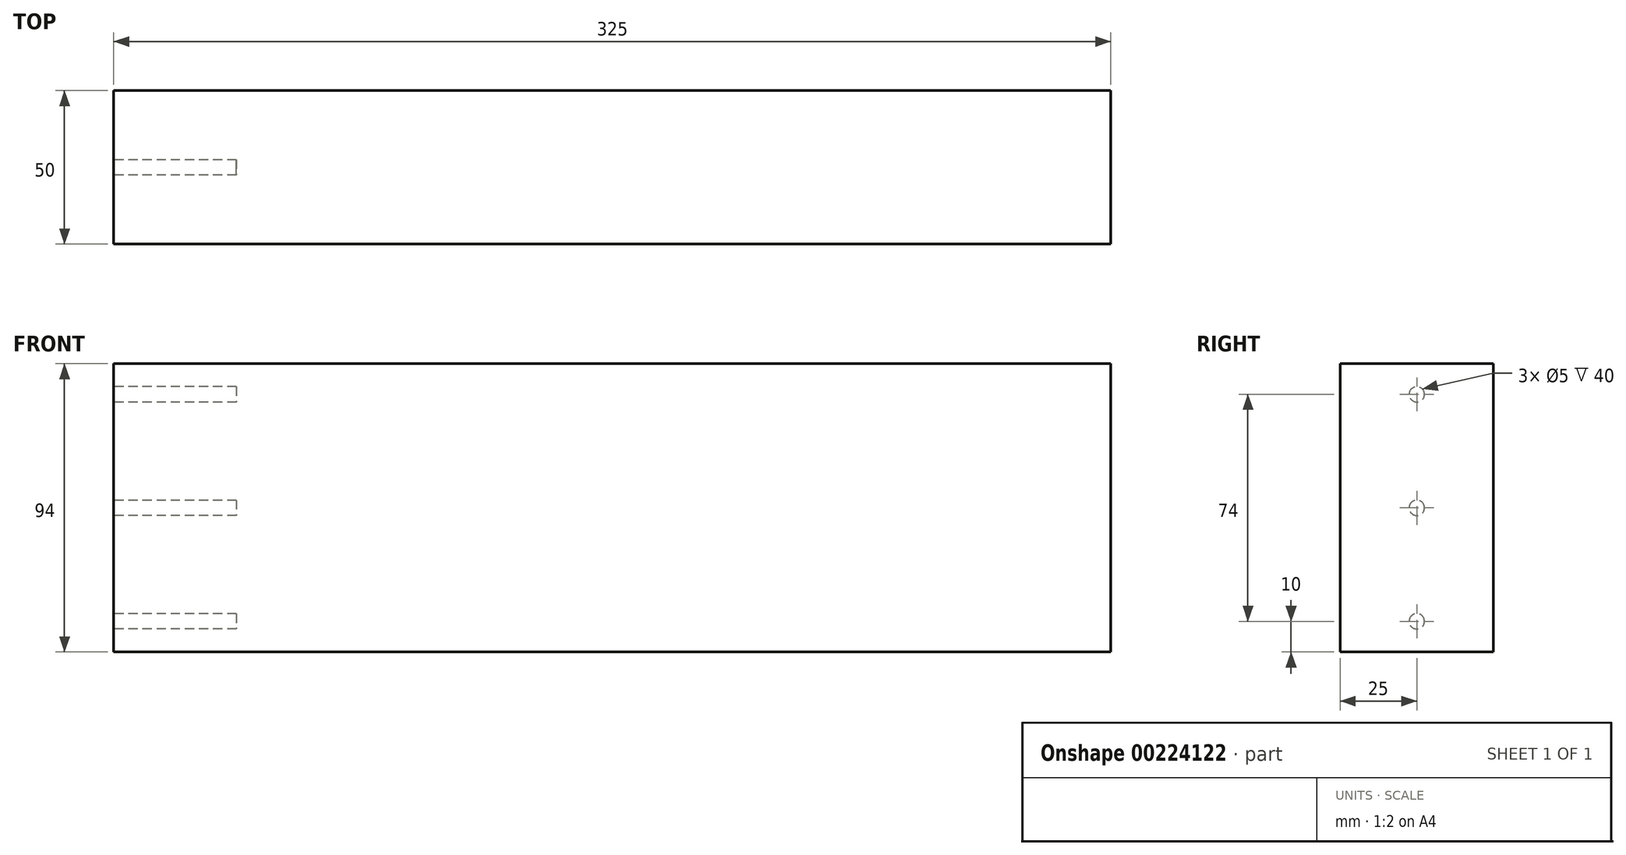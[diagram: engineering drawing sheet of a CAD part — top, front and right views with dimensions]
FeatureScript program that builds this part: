
annotation { "Feature Type Name" : "Feature", "Feature Type Description" : "" }
export const myFeature = defineFeature(function(context is Context, id is Id, definition is map)
    precondition{}
    {
        {
            var Q0;
            Q0=qCreatedBy(makeId("Front.planeOp"),FACE);
            var sketch = newSketch(context, id + "F2", { "sketchPlane" : qUnion([Q0])});
            skLineSegment(sketch, "E0.bottom", {"start": v(-162.5, -47) * mm, "end": v(162.5, -47) * mm});
            skLineSegment(sketch, "E0.top", {"start": v(-162.5, 47) * mm, "end": v(162.5, 47) * mm});
            skLineSegment(sketch, "E0.left", {"start": v(-162.5, -47) * mm, "end": v(-162.5, 47) * mm});
            skLineSegment(sketch, "E0.right", {"start": v(162.5, -47) * mm, "end": v(162.5, 47) * mm});
            skLineSegment(sketch, "E1", {"start": v(0, 47) * mm, "end": v(0, -47) * mm, "construction": true});
            skLineSegment(sketch, "E2", {"start": v(162.5, 0) * mm, "end": v(-162.5, 0) * mm, "construction": true});
            skSolve(sketch);
        }
        {
            var Q0;
            Q0=makeQuery(id+"F2.imprint","IMPRINT",FACE,{"disambiguationData":[TD([[makeQuery(id+"F2.imprint","IMPRINT",EDGE,{"derivedFrom":sQuery(id+"F2.wireOp",EDGE,"E0.bottom")}),1.0]])]});
            extrude(context, id + "F3", {"entities" : qUnion([Q0]), "endBound" : BoundingType.SYMMETRIC, "depth" : 50 * mm});
        }
        {
            var Q0;
            Q0=makeQuery(id+"F3.opExtrude","SWEPT_FACE",FACE,{"disambiguationData":[OSD([sQuery(id+"F2.wireOp",EDGE,"E0.left")])]});
            var sketch = newSketch(context, id + "F0", { "sketchPlane" : qUnion([Q0])});
            skCircle(sketch, "E3", {"center": v(0, 37) * mm, "radius": 2.5 * mm});
            skCircle(sketch, "E4", {"center": v(0, -37) * mm, "radius": 2.5 * mm});
            skCircle(sketch, "E5", {"center": v(0, 0) * mm, "radius": 2.5 * mm});
            skLineSegment(sketch, "E6", {"start": v(0, 47) * mm, "end": v(0, -47) * mm, "construction": true});
            skLineSegment(sketch, "E7", {"start": v(-25, 0) * mm, "end": v(25, 0) * mm, "construction": true});
            skLineSegment(sketch, "E8", {"start": v(25, 0) * mm, "end": v(25, 29.13) * mm, "construction": true});
            skSolve(sketch);
        }
        {
            var Q0;
            Q0=makeQuery(id+"F0.imprint","IMPRINT",FACE,{"disambiguationData":[TD([[makeQuery(id+"F0.imprint","IMPRINT",EDGE,{"derivedFrom":sQuery(id+"F0.wireOp",EDGE,"E4")}),1.0]])]});
            var Q1;
            Q1=makeQuery(id+"F0.imprint","IMPRINT",FACE,{"disambiguationData":[TD([[makeQuery(id+"F0.imprint","IMPRINT",EDGE,{"derivedFrom":sQuery(id+"F0.wireOp",EDGE,"E5")}),1.0]])]});
            var Q2;
            Q2=makeQuery(id+"F0.imprint","IMPRINT",FACE,{"disambiguationData":[TD([[makeQuery(id+"F0.imprint","IMPRINT",EDGE,{"derivedFrom":sQuery(id+"F0.wireOp",EDGE,"E3")}),1.0]])]});
            extrude(context, id + "F1", {"entities" : qUnion([Q0, Q1, Q2]), "operationType" : NewBodyOperationType.REMOVE, "oppositeDirection" : true, "depth" : 40 * mm});
        }
    });
